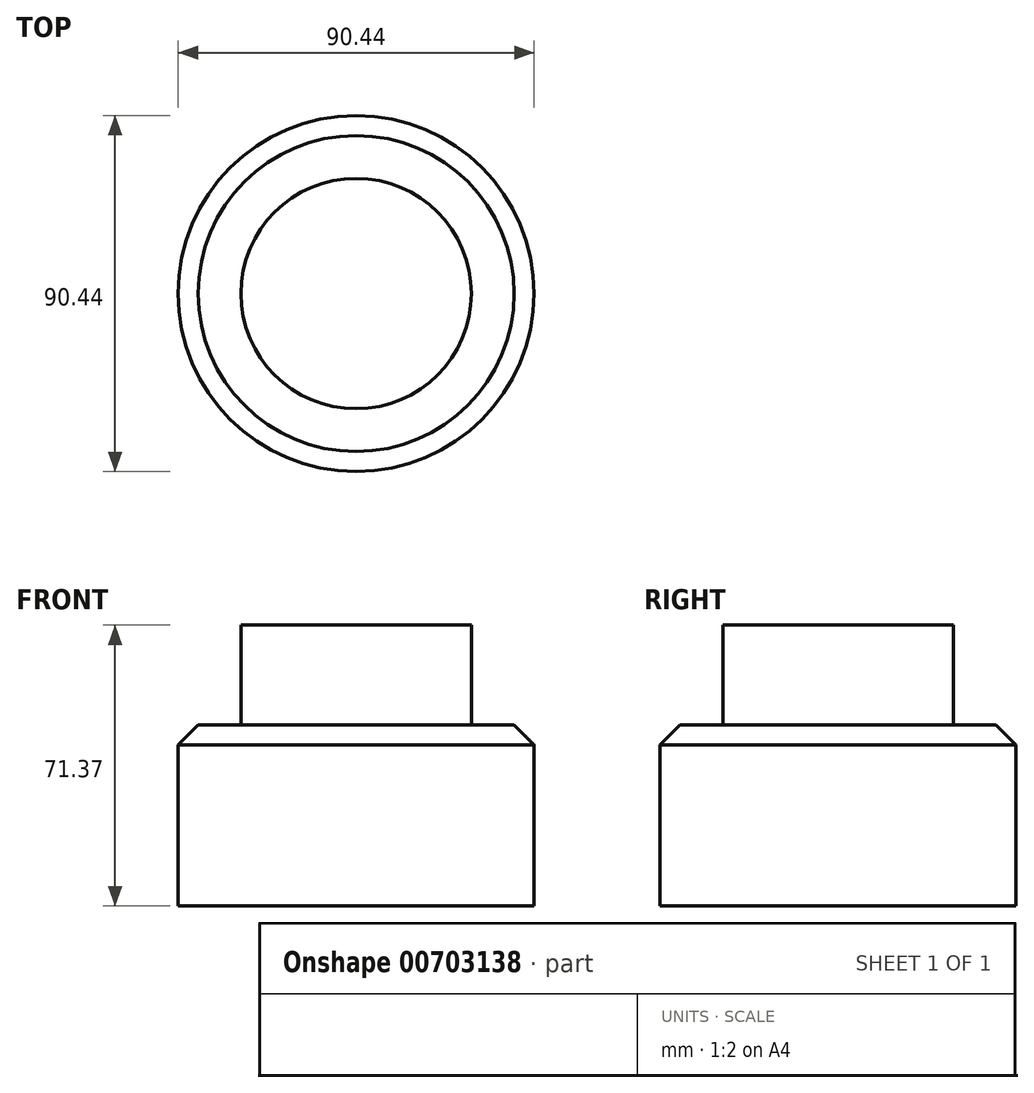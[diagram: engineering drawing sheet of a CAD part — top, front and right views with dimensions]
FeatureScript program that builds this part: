
annotation { "Feature Type Name" : "Feature", "Feature Type Description" : "" }
export const myFeature = defineFeature(function(context is Context, id is Id, definition is map)
    precondition{}
    {
        {
            var Q0;
            Q0=qCreatedBy(makeId("Top.planeOp"),FACE);
            var sketch = newSketch(context, id + "F0", { "sketchPlane" : qUnion([Q0])});
            skCircle(sketch, "E0", {"center": v(86.82, 0) * mm, "radius": 45.22 * mm});
            skSolve(sketch);
        }
        {
            var Q0;
            Q0 = qSketchRegion(id + "F0", true);
            extrude(context, id + "F1", {"entities" : qUnion([Q0]), "depth" : 45.97 * mm, "offsetDistance" : 25.4 * mm});
        }
        {
            var Q0;
            Q0=makeQuery(id+"F1.opExtrude","CAP_EDGE",EDGE,{"disambiguationData":[OSD([sQuery(id+"F0.wireOp",EDGE,"E0")])],"isStart":false});
            chamfer(context, id + "F2", {"entities" : qUnion([Q0]), "width" : 5.08 * mm, "tangentPropagation" : true});
        }
        {
            var Q0;
            Q0=makeQuery(id+"F1.opExtrude","CAP_FACE",FACE,{"disambiguationData":[OSD([sQuery(id+"F0.wireOp",EDGE,"E0")])],"isStart":false});
            var sketch = newSketch(context, id + "F3", { "sketchPlane" : qUnion([Q0])});
            skCircle(sketch, "E1", {"center": v(86.82, 0) * mm, "radius": 29.26 * mm});
            skSolve(sketch);
        }
        {
            var Q0;
            Q0 = qSketchRegion(id + "F3", true);
            extrude(context, id + "F4", {"entities" : qUnion([Q0]), "operationType" : NewBodyOperationType.ADD, "depth" : 25.4 * mm, "offsetDistance" : 25.4 * mm});
        }
    });
